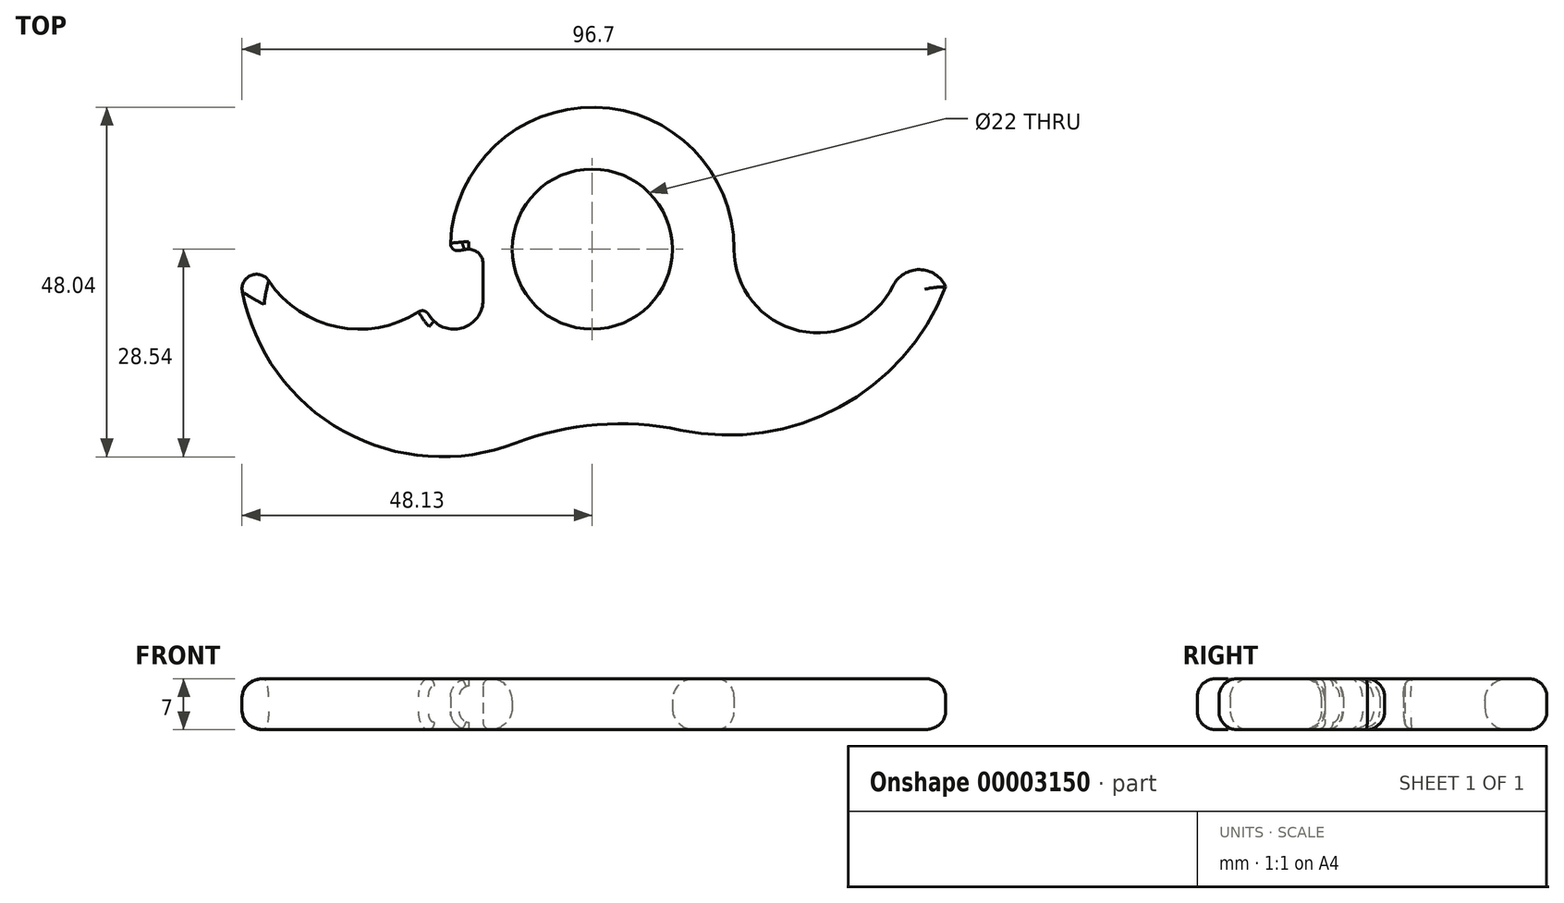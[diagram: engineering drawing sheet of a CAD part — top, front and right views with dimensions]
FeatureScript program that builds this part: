
annotation { "Feature Type Name" : "Feature", "Feature Type Description" : "" }
export const myFeature = defineFeature(function(context is Context, id is Id, definition is map)
    precondition{}
    {
        {
            var Q0;
            Q0=qCreatedBy(makeId("Top.planeOp"),FACE);
            var sketch = newSketch(context, id + "F0", { "sketchPlane" : qUnion([Q0])});
            skCircle(sketch, "E0", {"center": v(0, 0) * mm, "radius": 11 * mm});
            skArc(sketch, "E1", {"start": v(-15, -2) * mm, "mid": v(-15.71, -0.47) * mm, "end": v(-17.35, -0.03) * mm});
            skLineSegment(sketch, "E2", {"start": v(0, -11) * mm, "end": v(-57.76, -11) * mm, "construction": true});
            skLineSegment(sketch, "E3", {"start": v(0, -11) * mm, "end": v(50.25, -11) * mm, "construction": true});
            skArc(sketch, "E4", {"start": v(19.5, 0) * mm, "mid": v(28.4, -11.2) * mm, "end": v(41.33, -5.05) * mm});
            skLineSegment(sketch, "E5", {"start": v(0, 0) * mm, "end": v(31, 0) * mm, "construction": true});
            skArc(sketch, "E6", {"start": v(12.11, -24.87) * mm, "mid": v(33.96, -21.71) * mm, "end": v(48.57, -5.16) * mm});
            skArc(sketch, "E7", {"start": v(48.57, -5.16) * mm, "mid": v(44.98, -2.81) * mm, "end": v(41.33, -5.05) * mm});
            skLineSegment(sketch, "E8", {"start": v(31, 0) * mm, "end": v(31, 23.27) * mm, "construction": true});
            skLineSegment(sketch, "E9", {"start": v(-32, 28.17) * mm, "end": v(-32, -39.04) * mm, "construction": true});
            skLineSegment(sketch, "E10", {"start": v(0, 0) * mm, "end": v(-32, 0) * mm, "construction": true});
            skArc(sketch, "E11", {"start": v(-44.47, -4.34) * mm, "mid": v(-39.07, -9.23) * mm, "end": v(-32, -11) * mm});
            skArc(sketch, "E12", {"start": v(-48.1, -5.83) * mm, "mid": v(-34.19, -25.02) * mm, "end": v(-10.54, -26.67) * mm});
            skArc(sketch, "E13", {"start": v(12.11, -24.87) * mm, "mid": v(0.65, -24.13) * mm, "end": v(-10.54, -26.67) * mm});
            skArc(sketch, "E14", {"start": v(-44.47, -4.34) * mm, "mid": v(-46.9, -3.6) * mm, "end": v(-48.1, -5.83) * mm});
            skLineSegment(sketch, "E15", {"start": v(-17.35, -0.03) * mm, "end": v(-19.5, -0.4) * mm});
            skLineSegment(sketch, "E16", {"start": v(0, 0) * mm, "end": v(0, 43.06) * mm, "construction": true});
            skLineSegment(sketch, "E17", {"start": v(-17, -2) * mm, "end": v(-15, -2) * mm, "construction": true});
            skArc(sketch, "E18", {"start": v(-22.9, -7.92) * mm, "mid": v(-18.54, -10.97) * mm, "end": v(-15, -7) * mm});
            skArc(sketch, "E19.trimOffspring", {"start": v(19.5, 0) * mm, "mid": v(-0.2, 19.5) * mm, "end": v(-19.5, -0.4) * mm});
            skPoint(sketch, "E20.orphan", {"position": v(0, -19.5) * mm});
            skLineSegment(sketch, "E21", {"start": v(-15, -2) * mm, "end": v(-15, -7) * mm});
            skArc(sketch, "E22", {"start": v(-44.47, -4.34) * mm, "mid": v(-34.46, -10.8) * mm, "end": v(-22.9, -7.92) * mm});
            skArc(sketch, "E23.trimOffspring", {"start": v(-17.56, -0.07) * mm, "mid": v(-17.55, -0.03) * mm, "end": v(-17.54, 0) * mm});
            skSolve(sketch);
        }
        {
            var Q0;
            Q0 = qSketchRegion(id + "F0", true);
            extrude(context, id + "F1", {"entities" : qUnion([Q0]), "depth" : 7 * mm});
        }
        {
            var Q0;
            Q0=makeQuery(id+"F1.opExtrude","CAP_EDGE",EDGE,{"disambiguationData":[OSD([sQuery(id+"F0.wireOp",EDGE,"E22")])],"isStart":false});
            var Q1;
            Q1=makeQuery(id+"F1.opExtrude","CAP_EDGE",EDGE,{"disambiguationData":[OSD([sQuery(id+"F0.wireOp",EDGE,"E4")])],"isStart":false});
            var Q2;
            Q2=makeQuery(id+"F1.opExtrude","CAP_EDGE",EDGE,{"disambiguationData":[OSD([sQuery(id+"F0.wireOp",EDGE,"E12")])],"isStart":true});
            var Q3;
            Q3=makeQuery(id+"F1.opExtrude","CAP_EDGE",EDGE,{"disambiguationData":[OSD([sQuery(id+"F0.wireOp",EDGE,"E19.trimOffspring")])],"isStart":true});
            fillet(context, id + "F2", {"entities" : qUnion([Q0, Q1, Q2, Q3]), "radius" : 2.5 * mm, "tangentPropagation" : true, "allowEdgeOverflow" : false});
        }
        {
            var Q0;
            Q0=makeQuery(id+"F1.opExtrude","CAP_EDGE",EDGE,{"disambiguationData":[OSD([sQuery(id+"F0.wireOp",EDGE,"E0")])],"isStart":false});
            var Q1;
            Q1=makeQuery(id+"F1.opExtrude","CAP_EDGE",EDGE,{"disambiguationData":[OSD([sQuery(id+"F0.wireOp",EDGE,"E0")])],"isStart":true});
            fillet(context, id + "F3", {"entities" : qUnion([Q0, Q1]), "radius" : 3 * mm, "tangentPropagation" : true, "allowEdgeOverflow" : false});
        }
        {
            var Q0;
            Q0=makeQuery(id+"F1.opExtrude","CAP_EDGE",EDGE,{"disambiguationData":[OSD([sQuery(id+"F0.wireOp",EDGE,"E18")])],"isStart":false});
            fillet(context, id + "F4", {"entities" : qUnion([Q0]), "radius" : 1 * mm, "tangentPropagation" : true, "allowEdgeOverflow" : false});
        }
    });
